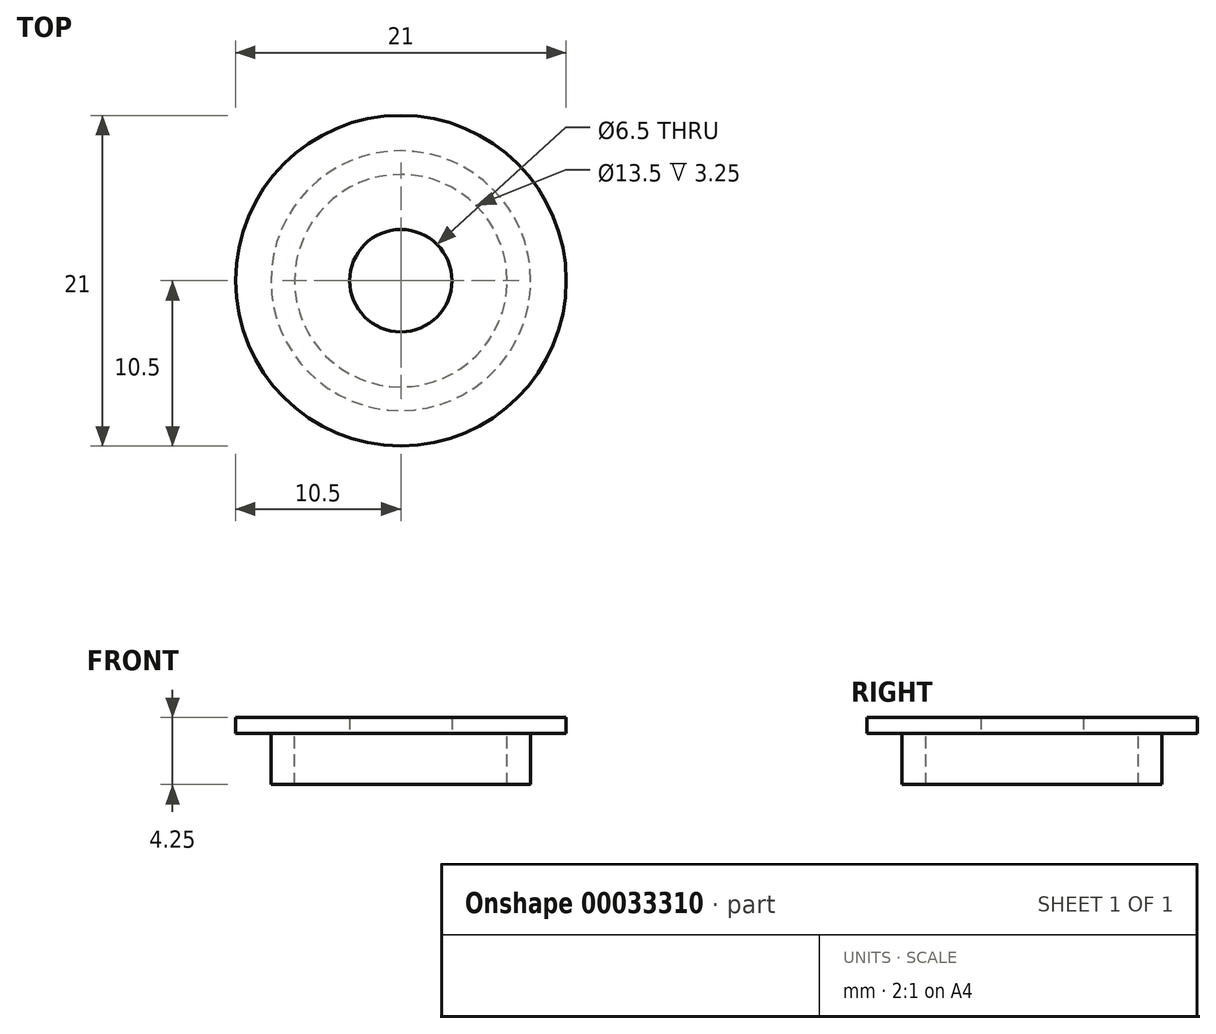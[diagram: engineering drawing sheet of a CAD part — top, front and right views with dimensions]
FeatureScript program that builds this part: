
annotation { "Feature Type Name" : "Feature", "Feature Type Description" : "" }
export const myFeature = defineFeature(function(context is Context, id is Id, definition is map)
    precondition{}
    {
        {
            var Q0;
            Q0=qCreatedBy(makeId("Top.planeOp"),FACE);
            var sketch = newSketch(context, id + "F0", { "sketchPlane" : qUnion([Q0])});
            skCircle(sketch, "E0", {"center": v(0, 0) * mm, "radius": 10.5 * mm});
            skCircle(sketch, "E1", {"center": v(0, 0) * mm, "radius": 3.25 * mm});
            skSolve(sketch);
        }
        {
            var Q0;
            Q0=makeQuery(id+"F0.imprint","IMPRINT",FACE,{"disambiguationData":[TD([[makeQuery(id+"F0.imprint","IMPRINT",EDGE,{"derivedFrom":sQuery(id+"F0.wireOp",EDGE,"E0")}),1.0]])]});
            extrude(context, id + "F1", {"entities" : qUnion([Q0]), "depth" : 1 * mm});
        }
        {
            var Q0;
            Q0=makeQuery(id+"F1.opExtrude","CAP_FACE",FACE,{"disambiguationData":[OSD([sQuery(id+"F0.wireOp",EDGE,"E0"),sQuery(id+"F0.wireOp",EDGE,"E1")])],"isStart":true});
            var sketch = newSketch(context, id + "F2", { "sketchPlane" : qUnion([Q0])});
            skCircle(sketch, "E2", {"center": v(0, 0) * mm, "radius": 6.75 * mm});
            skCircle(sketch, "E3", {"center": v(0, 0) * mm, "radius": 8.25 * mm});
            skSolve(sketch);
        }
        {
            var Q0;
            Q0=makeQuery(id+"F2.imprint","IMPRINT",FACE,{"disambiguationData":[TD([[makeQuery(id+"F2.imprint","IMPRINT",EDGE,{"derivedFrom":sQuery(id+"F2.wireOp",EDGE,"E2")}),-1.0]])]});
            extrude(context, id + "F3", {"entities" : qUnion([Q0]), "operationType" : NewBodyOperationType.ADD, "depth" : 3.25 * mm});
        }
    });
